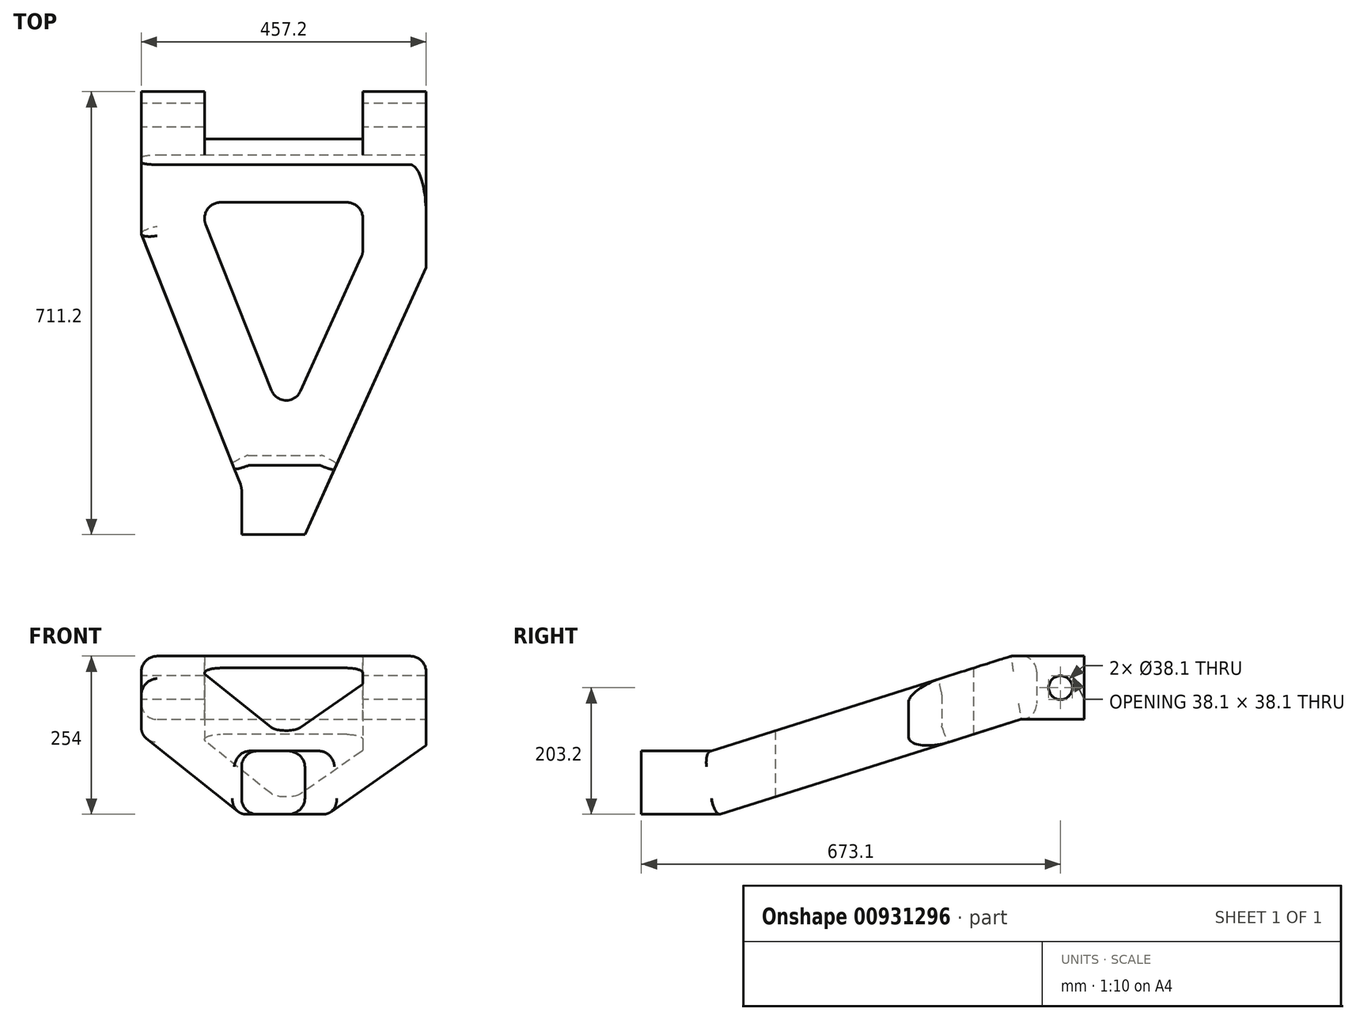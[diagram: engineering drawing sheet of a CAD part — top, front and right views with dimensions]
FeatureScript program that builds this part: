
annotation { "Feature Type Name" : "Feature", "Feature Type Description" : "" }
export const myFeature = defineFeature(function(context is Context, id is Id, definition is map)
    precondition{}
    {
        {
            var Q0;
            Q0=qCreatedBy(makeId("Top.planeOp"),FACE);
            var sketch = newSketch(context, id + "F0", { "sketchPlane" : qUnion([Q0])});
            skLineSegment(sketch, "E0.top", {"start": v(228.6, 355.6) * mm, "end": v(127, 355.6) * mm});
            skLineSegment(sketch, "E0.left", {"start": v(228.6, 73.27) * mm, "end": v(228.6, 355.6) * mm});
            skLineSegment(sketch, "E0.right", {"start": v(-228.6, 127) * mm, "end": v(-228.6, 355.6) * mm});
            skPoint(sketch, "E0.middle", {"position": v(0, 0) * mm});
            skLineSegment(sketch, "E1", {"start": v(-127, 355.6) * mm, "end": v(-127, 279.4) * mm});
            skLineSegment(sketch, "E2", {"start": v(127, 355.6) * mm, "end": v(127, 279.4) * mm});
            skLineSegment(sketch, "E3", {"start": v(-127, 279.4) * mm, "end": v(127, 279.4) * mm});
            skLineSegment(sketch, "E4.trimOffspring", {"start": v(-127, 355.6) * mm, "end": v(-228.6, 355.6) * mm});
            skLineSegment(sketch, "E5", {"start": v(-228.6, 127) * mm, "end": v(-69.35, -274.9) * mm});
            skLineSegment(sketch, "E6", {"start": v(-67.57, -284.25) * mm, "end": v(-67.57, -355.6) * mm});
            skLineSegment(sketch, "E7", {"start": v(-67.57, -355.6) * mm, "end": v(34.03, -355.6) * mm});
            skLineSegment(sketch, "E8", {"start": v(34.03, -355.6) * mm, "end": v(228.6, 73.27) * mm});
            skPoint(sketch, "E9.orphan", {"position": v(228.6, -355.6) * mm});
            skPoint(sketch, "E0.bottom.end.orphan", {"position": v(-228.6, -355.6) * mm});
            skLineSegment(sketch, "E10.0", {"start": v(127, 100.73) * mm, "end": v(127, 152.4) * mm});
            skLineSegment(sketch, "E10.1", {"start": v(-101.6, 177.8) * mm, "end": v(101.6, 177.8) * mm});
            skLineSegment(sketch, "E10.2", {"start": v(26.95, -125.3) * mm, "end": v(124.73, 90.23) * mm});
            skLineSegment(sketch, "E10.3", {"start": v(-125.21, 141.89) * mm, "end": v(-19.8, -124.16) * mm});
            skLineSegment(sketch, "E10.4", {"start": v(-127, 151.24) * mm, "end": v(-127, 152.4) * mm});
            skPoint(sketch, "E11.visualSharp", {"position": v(2.24, -179.76) * mm});
            skArc(sketch, "E11.filletArc", {"start": v(-19.8, -124.16) * mm, "mid": v(3.2, -140.2) * mm, "end": v(26.95, -125.3) * mm});
            skPoint(sketch, "E12.visualSharp", {"position": v(-127, 177.8) * mm});
            skArc(sketch, "E12.filletArc", {"start": v(-101.6, 177.8) * mm, "mid": v(-119.56, 170.36) * mm, "end": v(-127, 152.4) * mm});
            skPoint(sketch, "E13.visualSharp", {"position": v(127, 177.8) * mm});
            skArc(sketch, "E13.filletArc", {"start": v(127, 152.4) * mm, "mid": v(119.56, 170.36) * mm, "end": v(101.6, 177.8) * mm});
            skPoint(sketch, "E14.visualSharp", {"position": v(127, 95.24) * mm});
            skArc(sketch, "E14.filletArc", {"start": v(124.73, 90.23) * mm, "mid": v(126.43, 95.36) * mm, "end": v(127, 100.73) * mm});
            skPoint(sketch, "E15.visualSharp", {"position": v(-127, 146.4) * mm});
            skArc(sketch, "E15.filletArc", {"start": v(-127, 151.24) * mm, "mid": v(-126.55, 146.48) * mm, "end": v(-125.21, 141.89) * mm});
            skPoint(sketch, "E16.visualSharp", {"position": v(-67.57, -279.4) * mm});
            skArc(sketch, "E16.filletArc", {"start": v(-67.57, -284.25) * mm, "mid": v(-68.02, -279.49) * mm, "end": v(-69.35, -274.9) * mm});
            skSolve(sketch);
        }
        {
            var Q0;
            Q0=makeQuery(id+"F0.imprint","IMPRINT",FACE,{"disambiguationData":[TD([[makeQuery(id+"F0.imprint","IMPRINT",EDGE,{"derivedFrom":sQuery(id+"F0.wireOp",EDGE,"E0.top")}),1.0]])]});
            extrude(context, id + "F1", {"entities" : qUnion([Q0]), "endBound" : BoundingType.SYMMETRIC, "depth" : 254 * mm, "offsetDistance" : 25.4 * mm});
        }
        {
            var Q0;
            Q0=makeQuery(id+"F1.opExtrude","SWEPT_FACE",FACE,{"disambiguationData":[OSD([sQuery(id+"F0.wireOp",EDGE,"E0.left")])]});
            var sketch = newSketch(context, id + "F2", { "sketchPlane" : qUnion([Q0])});
            skLineSegment(sketch, "E17", {"start": v(-355.6, -127) * mm, "end": v(-228.6, -127) * mm});
            skLineSegment(sketch, "E18", {"start": v(355.6, 127) * mm, "end": v(355.6, 25.4) * mm});
            skLineSegment(sketch, "E19", {"start": v(-355.6, -127) * mm, "end": v(-355.6, -25.4) * mm});
            skLineSegment(sketch, "E20", {"start": v(355.6, 25.4) * mm, "end": v(254, 25.4) * mm});
            skLineSegment(sketch, "E21", {"start": v(-228.6, -127) * mm, "end": v(254, 25.4) * mm});
            skLineSegment(sketch, "E22", {"start": v(-355.6, -25.4) * mm, "end": v(-399.75, -25.4) * mm});
            skLineSegment(sketch, "E23", {"start": v(-399.75, -25.4) * mm, "end": v(-399.75, -182.48) * mm});
            skLineSegment(sketch, "E24", {"start": v(-399.75, -182.48) * mm, "end": v(403.13, -182.48) * mm});
            skLineSegment(sketch, "E25", {"start": v(403.13, -182.48) * mm, "end": v(403.13, 126.77) * mm});
            skLineSegment(sketch, "E26", {"start": v(403.13, 126.77) * mm, "end": v(355.6, 127) * mm});
            skSolve(sketch);
        }
        {
            var Q0;
            Q0 = qSketchRegion(id + "F2", true);
            extrude(context, id + "F3", {"entities" : qUnion([Q0]), "operationType" : NewBodyOperationType.REMOVE, "oppositeDirection" : true, "depth" : 627.38 * mm, "offsetDistance" : 25.4 * mm});
        }
        {
            var Q0;
            Q0=makeQuery(id+"F1.opExtrude","SWEPT_FACE",FACE,{"disambiguationData":[OSD([sQuery(id+"F0.wireOp",EDGE,"E0.left")])]});
            var sketch = newSketch(context, id + "F4", { "sketchPlane" : qUnion([Q0])});
            skLineSegment(sketch, "E27.0", {"start": v(355.6, 127) * mm, "end": v(238.34, 127) * mm});
            skLineSegment(sketch, "E27.1", {"start": v(42.67, 65.21) * mm, "end": v(238.34, 127) * mm});
            skLineSegment(sketch, "E27.2", {"start": v(42.67, 65.21) * mm, "end": v(-244.26, -25.4) * mm});
            skLineSegment(sketch, "E27.3", {"start": v(-355.6, -25.4) * mm, "end": v(-244.26, -25.4) * mm});
            skLineSegment(sketch, "E28", {"start": v(-355.6, -25.4) * mm, "end": v(-388.33, 150.27) * mm});
            skLineSegment(sketch, "E29", {"start": v(-388.33, 150.27) * mm, "end": v(355.6, 150.27) * mm});
            skLineSegment(sketch, "E30", {"start": v(355.6, 150.27) * mm, "end": v(355.6, 127) * mm});
            skSolve(sketch);
        }
        {
            var Q0;
            Q0 = qSketchRegion(id + "F4", true);
            extrude(context, id + "F5", {"entities" : qUnion([Q0]), "operationType" : NewBodyOperationType.REMOVE, "oppositeDirection" : true, "depth" : 546.1 * mm, "offsetDistance" : 25.4 * mm});
        }
        {
            var Q0;
            Q0=makeQuery(id+"F1.opExtrude","SWEPT_FACE",FACE,{"disambiguationData":[OSD([sQuery(id+"F0.wireOp",EDGE,"E1")])]});
            var sketch = newSketch(context, id + "F6", { "sketchPlane" : qUnion([Q0])});
            skCircle(sketch, "E31", {"center": v(317.5, 76.2) * mm, "radius": 19.05 * mm});
            skPoint(sketch, "E31.centerSnap0", {"position": v(317.5, 25.4) * mm});
            skPoint(sketch, "E31.centerSnap1", {"position": v(355.6, 76.2) * mm});
            skSolve(sketch);
        }
        {
            var Q0;
            Q0 = qSketchRegion(id + "F6", true);
            extrude(context, id + "F7", {"entities" : qUnion([Q0]), "operationType" : NewBodyOperationType.REMOVE, "endBound" : BoundingType.SYMMETRIC, "depth" : 819.9 * mm, "offsetDistance" : 25.4 * mm});
        }
        {
            var Q0;
            Q0=makeQuery(id+"F5.boolean.opBoolean","INTERSECT",EDGE,{"derivedFrom":[makeQuery(id+"F1.opExtrude","SWEPT_FACE",FACE,{"disambiguationData":[OSD([sQuery(id+"F0.wireOp",EDGE,"E8")])]}),makeQuery(id+"F5.opExtrude","SWEPT_FACE",FACE,{"disambiguationData":[OSD([sQuery(id+"F4.wireOp",EDGE,"E27.1"),sQuery(id+"F4.wireOp",EDGE,"E27.2")])]})]});
            var Q1;
            Q1=makeQuery(id+"F5.boolean.opBoolean","COPY",EDGE,{"derivedFrom":makeQuery(id+"F5.opExtrude","CAP_EDGE",EDGE,{"disambiguationData":[OSD([sQuery(id+"F4.wireOp",EDGE,"E27.1"),sQuery(id+"F4.wireOp",EDGE,"E27.2")])],"isStart":true})});
            var Q2;
            Q2=makeQuery(id+"F1.opExtrude","CAP_EDGE",EDGE,{"disambiguationData":[OSD([sQuery(id+"F0.wireOp",EDGE,"E0.left")])],"isStart":false});
            var Q3;
            Q3=makeQuery(id+"F5.boolean.opBoolean","INTERSECT",EDGE,{"derivedFrom":[makeQuery(id+"F1.opExtrude","SWEPT_FACE",FACE,{"disambiguationData":[OSD([sQuery(id+"F0.wireOp",EDGE,"E8")])]}),makeQuery(id+"F5.opExtrude","SWEPT_FACE",FACE,{"disambiguationData":[OSD([sQuery(id+"F4.wireOp",EDGE,"E27.3")])]})]});
            var Q4;
            Q4=makeQuery(id+"F5.boolean.opBoolean","INTERSECT",EDGE,{"derivedFrom":[makeQuery(id+"F1.opExtrude","SWEPT_FACE",FACE,{"disambiguationData":[OSD([sQuery(id+"F0.wireOp",EDGE,"E6")])]}),makeQuery(id+"F5.opExtrude","SWEPT_FACE",FACE,{"disambiguationData":[OSD([sQuery(id+"F4.wireOp",EDGE,"E27.3")])]})]});
            var Q5;
            Q5=makeQuery(id+"F5.boolean.opBoolean","INTERSECT",EDGE,{"derivedFrom":[makeQuery(id+"F1.opExtrude","SWEPT_FACE",FACE,{"disambiguationData":[OSD([sQuery(id+"F0.wireOp",EDGE,"E5")])]}),makeQuery(id+"F5.opExtrude","SWEPT_FACE",FACE,{"disambiguationData":[OSD([sQuery(id+"F4.wireOp",EDGE,"E27.1"),sQuery(id+"F4.wireOp",EDGE,"E27.2")])]})]});
            var Q6;
            Q6=makeQuery(id+"F5.boolean.opBoolean","INTERSECT",EDGE,{"derivedFrom":[makeQuery(id+"F1.opExtrude","SWEPT_FACE",FACE,{"disambiguationData":[OSD([sQuery(id+"F0.wireOp",EDGE,"E0.right")])]}),makeQuery(id+"F5.opExtrude","SWEPT_FACE",FACE,{"disambiguationData":[OSD([sQuery(id+"F4.wireOp",EDGE,"E27.1"),sQuery(id+"F4.wireOp",EDGE,"E27.2")])]})]});
            var Q7;
            Q7=makeQuery(id+"F1.opExtrude","CAP_EDGE",EDGE,{"disambiguationData":[OSD([sQuery(id+"F0.wireOp",EDGE,"E0.right")])],"isStart":false});
            var Q8;
            Q8=makeQuery(id+"F3.boolean.opBoolean","INTERSECT",EDGE,{"derivedFrom":[makeQuery(id+"F1.opExtrude","SWEPT_FACE",FACE,{"disambiguationData":[OSD([sQuery(id+"F0.wireOp",EDGE,"E0.right")])]}),makeQuery(id+"F3.opExtrude","SWEPT_FACE",FACE,{"disambiguationData":[OSD([sQuery(id+"F2.wireOp",EDGE,"E20")])]})]});
            var Q9;
            Q9=makeQuery(id+"F3.boolean.opBoolean","INTERSECT",EDGE,{"derivedFrom":[makeQuery(id+"F1.opExtrude","SWEPT_FACE",FACE,{"disambiguationData":[OSD([sQuery(id+"F0.wireOp",EDGE,"E0.right")])]}),makeQuery(id+"F3.opExtrude","SWEPT_FACE",FACE,{"disambiguationData":[OSD([sQuery(id+"F2.wireOp",EDGE,"E21")])]})]});
            var Q10;
            Q10=makeQuery(id+"F3.boolean.opBoolean","INTERSECT",EDGE,{"derivedFrom":[makeQuery(id+"F1.opExtrude","SWEPT_FACE",FACE,{"disambiguationData":[OSD([sQuery(id+"F0.wireOp",EDGE,"E5")])]}),makeQuery(id+"F3.opExtrude","SWEPT_FACE",FACE,{"disambiguationData":[OSD([sQuery(id+"F2.wireOp",EDGE,"E21")])]})]});
            var Q11;
            Q11=makeQuery(id+"F1.opExtrude","CAP_EDGE",EDGE,{"disambiguationData":[OSD([sQuery(id+"F0.wireOp",EDGE,"E5")])],"isStart":true});
            var Q12;
            Q12=makeQuery(id+"F1.opExtrude","CAP_EDGE",EDGE,{"disambiguationData":[OSD([sQuery(id+"F0.wireOp",EDGE,"E6")])],"isStart":true});
            var Q13;
            Q13=makeQuery(id+"F3.boolean.opBoolean","INTERSECT",EDGE,{"derivedFrom":[makeQuery(id+"F1.opExtrude","SWEPT_FACE",FACE,{"disambiguationData":[OSD([sQuery(id+"F0.wireOp",EDGE,"E8")])]}),makeQuery(id+"F3.opExtrude","SWEPT_FACE",FACE,{"disambiguationData":[OSD([sQuery(id+"F2.wireOp",EDGE,"E21")])]})]});
            var Q14;
            Q14=makeQuery(id+"F1.opExtrude","CAP_EDGE",EDGE,{"disambiguationData":[OSD([sQuery(id+"F0.wireOp",EDGE,"E8")])],"isStart":true});
            var Q15;
            Q15=makeQuery(id+"F3.boolean.opBoolean","COPY",EDGE,{"derivedFrom":makeQuery(id+"F3.opExtrude","CAP_EDGE",EDGE,{"disambiguationData":[OSD([sQuery(id+"F2.wireOp",EDGE,"E21")])],"isStart":true})});
            var Q16;
            Q16=makeQuery(id+"F3.boolean.opBoolean","COPY",EDGE,{"derivedFrom":makeQuery(id+"F3.opExtrude","CAP_EDGE",EDGE,{"disambiguationData":[OSD([sQuery(id+"F2.wireOp",EDGE,"E20")])],"isStart":true})});
            var Q17;
            Q17=makeQuery(id+"F1.opExtrude","CAP_EDGE",EDGE,{"disambiguationData":[OSD([sQuery(id+"F0.wireOp",EDGE,"E3")])],"isStart":false});
            var Q18;
            Q18=makeQuery(id+"F3.boolean.opBoolean","INTERSECT",EDGE,{"derivedFrom":[makeQuery(id+"F1.opExtrude","SWEPT_FACE",FACE,{"disambiguationData":[OSD([sQuery(id+"F0.wireOp",EDGE,"E3")])]}),makeQuery(id+"F3.opExtrude","SWEPT_FACE",FACE,{"disambiguationData":[OSD([sQuery(id+"F2.wireOp",EDGE,"E20")])]})]});
            fillet(context, id + "F8", {"entities" : qUnion([Q0, Q1, Q2, Q3, Q4, Q5, Q6, Q7, Q8, Q9, Q10, Q11, Q12, Q13, Q14, Q15, Q16, Q17, Q18]), "radius" : 25.4 * mm, "tangentPropagation" : true, "allowEdgeOverflow" : false});
        }
    });
